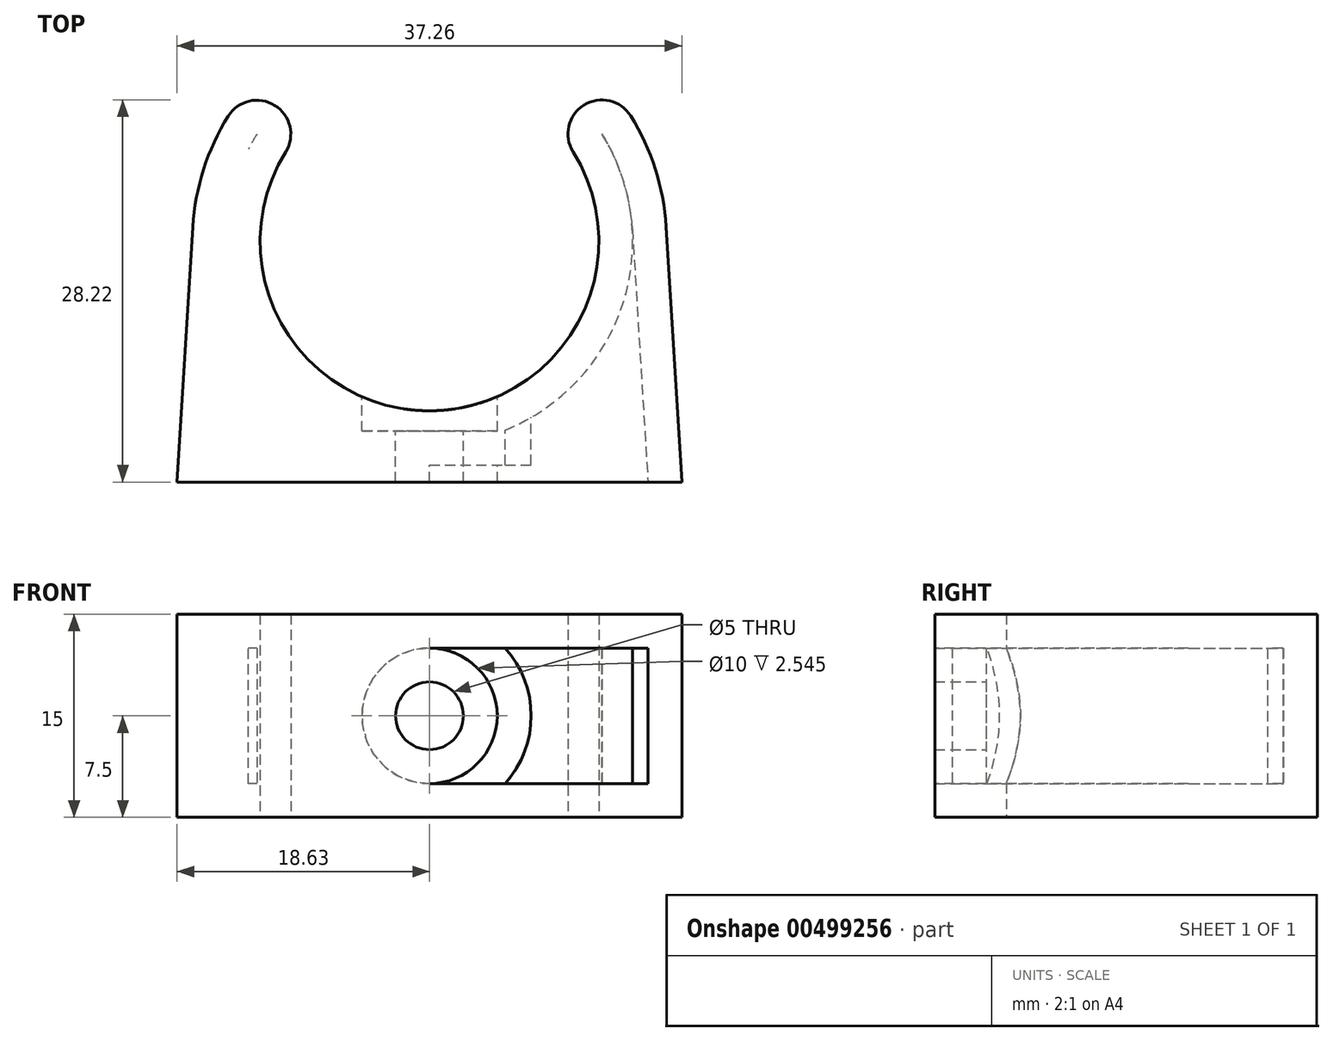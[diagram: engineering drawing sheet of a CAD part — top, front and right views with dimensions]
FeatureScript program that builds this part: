
annotation { "Feature Type Name" : "Feature", "Feature Type Description" : "" }
export const myFeature = defineFeature(function(context is Context, id is Id, definition is map)
    precondition{}
    {
        {
            var Q0;
            Q0=qCreatedBy(makeId("Top.planeOp"),FACE);
            var sketch = newSketch(context, id + "F0", { "sketchPlane" : qUnion([Q0])});
            skArc(sketch, "E0", {"start": v(-10.61, 35.42) * mm, "mid": v(0, 16.31) * mm, "end": v(10.6, 35.43) * mm});
            skArc(sketch, "E1.0", {"start": v(-14.86, 38.06) * mm, "mid": v(-16.67, 34.13) * mm, "end": v(-17.47, 29.89) * mm});
            skLineSegment(sketch, "E2", {"start": v(-17.47, 29.89) * mm, "end": v(-18.63, 11.04) * mm});
            skLineSegment(sketch, "E3", {"start": v(17.47, 29.89) * mm, "end": v(18.63, 11.04) * mm});
            skArc(sketch, "E4.trimOffspring", {"start": v(17.47, 29.89) * mm, "mid": v(16.67, 34.15) * mm, "end": v(14.85, 38.08) * mm});
            skPoint(sketch, "E5.endSnap0", {"position": v(-14.18, 39.07) * mm});
            skPoint(sketch, "E6.orphan", {"position": v(-14.18, 43.96) * mm});
            skArc(sketch, "E7", {"start": v(-11.96, 41.59) * mm, "mid": v(-11.95, 41.6) * mm, "end": v(-11.95, 41.6) * mm});
            skLineSegment(sketch, "E8", {"start": v(-18.63, 11.04) * mm, "end": v(18.63, 11.04) * mm});
            skPoint(sketch, "E9.start.orphan", {"position": v(-30.47, 0) * mm});
            skPoint(sketch, "E10.start.orphan", {"position": v(-19.3, 0) * mm});
            skPoint(sketch, "E11.orphan", {"position": v(19.3, 0) * mm});
            skPoint(sketch, "E12.end.orphan", {"position": v(-30.8, 41.59) * mm});
            skArc(sketch, "E13", {"start": v(-14.86, 38.06) * mm, "mid": v(-11.42, 38.86) * mm, "end": v(-10.61, 35.42) * mm});
            skArc(sketch, "E14", {"start": v(10.6, 35.43) * mm, "mid": v(11.4, 38.88) * mm, "end": v(14.85, 38.08) * mm});
            skSolve(sketch);
        }
        {
            var Q0;
            Q0=makeQuery(id+"F0.imprint","IMPRINT",FACE,{"disambiguationData":[TD([[makeQuery(id+"F0.imprint","IMPRINT",EDGE,{"derivedFrom":sQuery(id+"F0.wireOp",EDGE,"E0")}),-1.0]])]});
            extrude(context, id + "F1", {"entities" : qUnion([Q0]), "depth" : 15 * mm});
        }
        {
            var Q0;
            Q0=makeQuery(id+"F1.opExtrude","SWEPT_FACE",FACE,{"disambiguationData":[OSD([sQuery(id+"F0.wireOp",EDGE,"E0")])]});
            var Q1;
            Q1=qCreatedBy(makeId("Front.planeOp"),FACE);
            cPlane(context, id + "F2", {"entities" : qUnion([Q0, Q1]), "cplaneType" : CPlaneType.LINE_ANGLE, "offset" : 25 * mm, "angle" : 0 * degree, "width" : 150 * mm, "height" : 150 * mm});
        }
        {
            var Q0;
            Q0=qCreatedBy(id+"F2.planeOp",FACE);
            var sketch = newSketch(context, id + "F3", { "sketchPlane" : qUnion([Q0])});
            skPoint(sketch, "E15", {"position": v(0, 0) * mm});
            skLineSegment(sketch, "E16", {"start": v(0, 0) * mm, "end": v(0, 7.5) * mm});
            skSolve(sketch);
        }
        {
            var Q0;
            Q0=sQuery(id+"F3.wireOp",VERTEX,"E16.end");
            var Q1;
            Q1=makeQuery(id+"F1.opExtrude","SWEPT_BODY",BODY,{"disambiguationData":[OSD([sQuery(id+"F0.wireOp",EDGE,"E0"),sQuery(id+"F0.wireOp",EDGE,"E1.0"),sQuery(id+"F0.wireOp",EDGE,"E2"),sQuery(id+"F0.wireOp",EDGE,"E3"),sQuery(id+"F0.wireOp",EDGE,"E4.trimOffspring"),sQuery(id+"F0.wireOp",EDGE,"E7"),sQuery(id+"F0.wireOp",EDGE,"2ab29c43-b577-4fc3-a5a4-e39ccbc7b5ff"),sQuery(id+"F0.wireOp",EDGE,"E8")])]});
            hole(context, id + "F4", {"style" : HoleStyle.C_BORE, "endStyle" : HoleEndStyle.THROUGH, "holeDiameter" : 5 * mm, "cBoreDiameter" : 10 * mm, "cBoreDepth" : 1.5 * mm, "isTappedThrough" : true, "tappedDepth" : 12 * mm, "tapClearance" : 3, "locations" : qUnion([Q0]), "scope" : qUnion([Q1])});
        }
        {
            var Q0;
            Q0=makeQuery(id+"F1.opExtrude","SWEPT_FACE",FACE,{"disambiguationData":[OSD([sQuery(id+"F0.wireOp",EDGE,"E8")])]});
            shell(context, id + "F5", {"entities" : qUnion([Q0]), "thickness" : 2.5 * mm});
        }
    });
